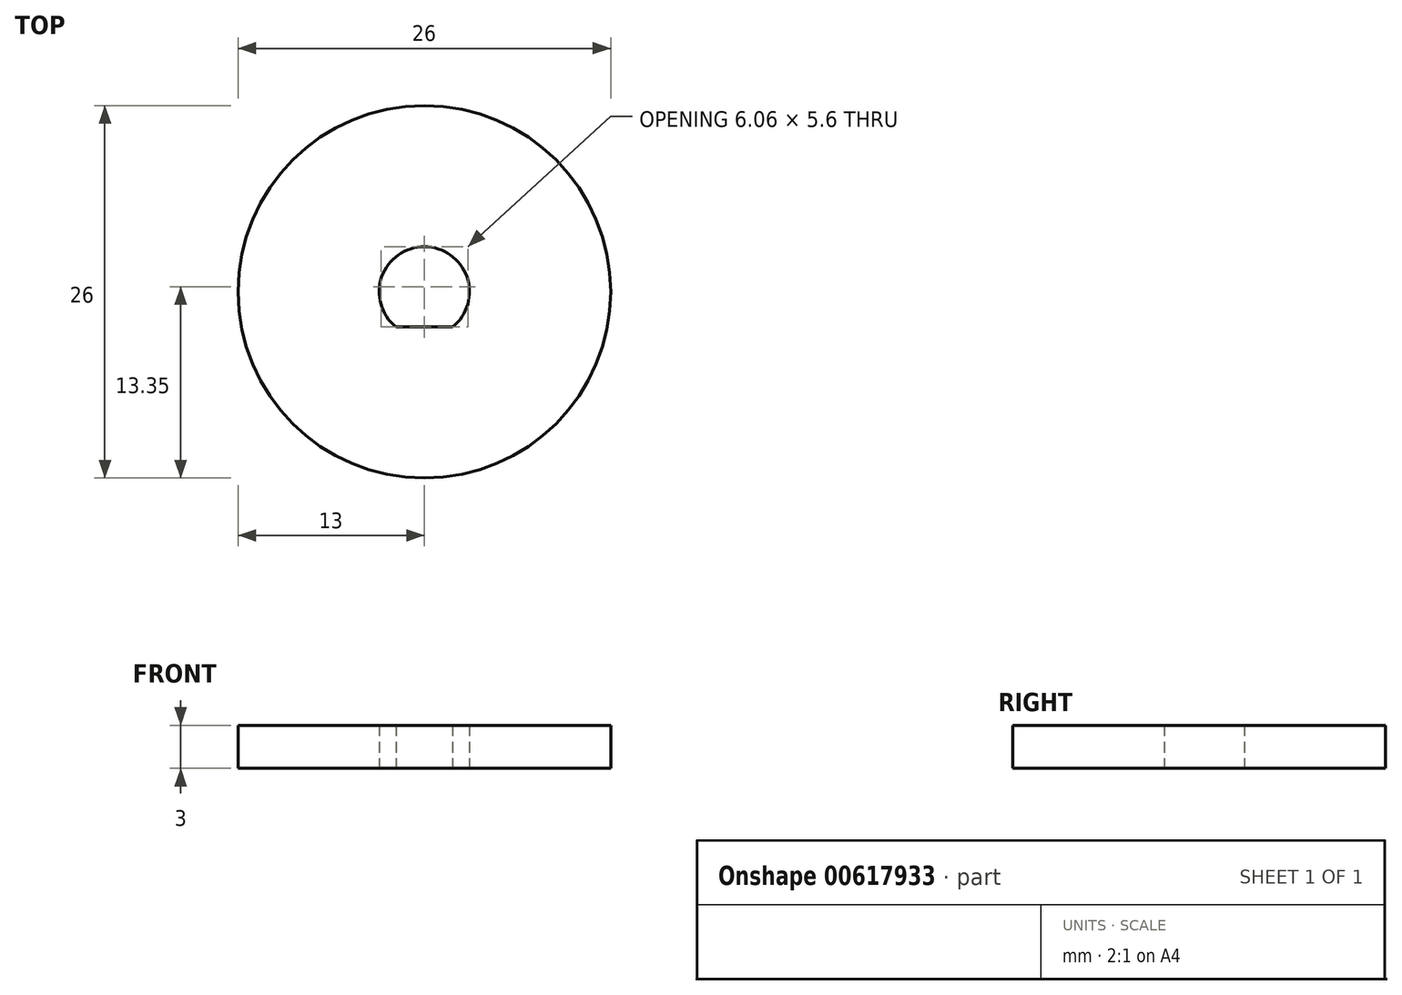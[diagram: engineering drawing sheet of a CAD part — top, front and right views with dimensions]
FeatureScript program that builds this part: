
annotation { "Feature Type Name" : "Feature", "Feature Type Description" : "" }
export const myFeature = defineFeature(function(context is Context, id is Id, definition is map)
    precondition{}
    {
        {
            var Q0;
            Q0=qCreatedBy(makeId("Top.planeOp"),FACE);
            var sketch = newSketch(context, id + "F0", { "sketchPlane" : qUnion([Q0])});
            skArc(sketch, "E0", {"start": v(1.98, -2.45) * mm, "mid": v(0, 3.15) * mm, "end": v(-1.98, -2.45) * mm});
            skLineSegment(sketch, "E1", {"start": v(0, 3.15) * mm, "end": v(0, -2.45) * mm, "construction": true});
            skLineSegment(sketch, "E2", {"start": v(-1.98, -2.45) * mm, "end": v(1.98, -2.45) * mm});
            skCircle(sketch, "E3", {"center": v(0, 0) * mm, "radius": 13 * mm});
            skSolve(sketch);
        }
        {
            var Q0;
            Q0 = qSketchRegion(id + "F0", true);
            extrude(context, id + "F1", {"entities" : qUnion([Q0]), "depth" : 3 * mm, "offsetDistance" : 25 * mm});
        }
    });
